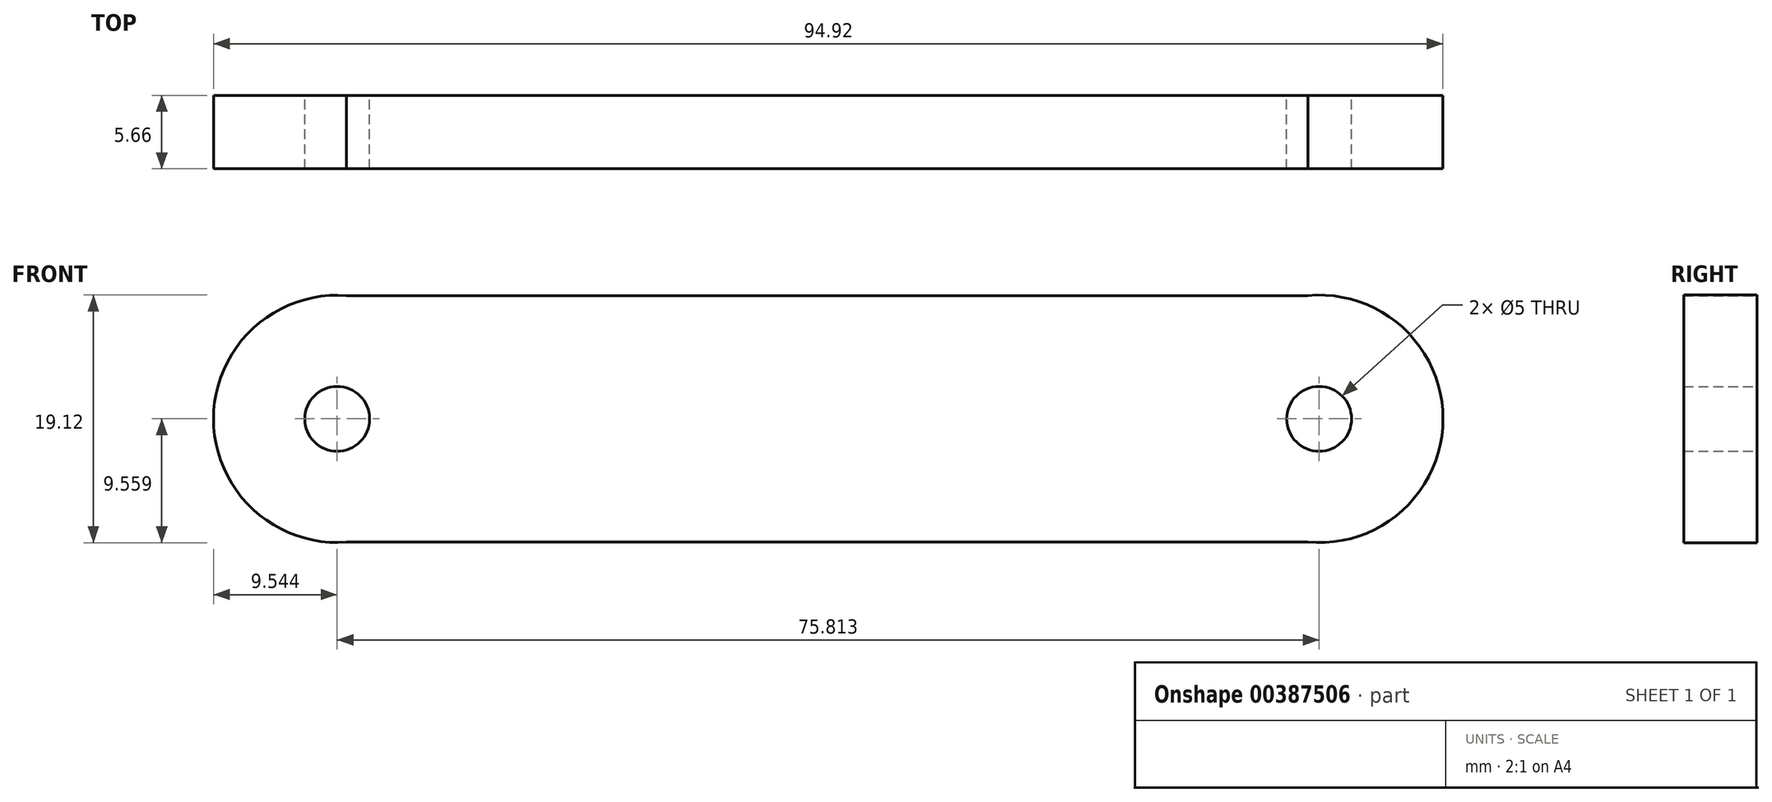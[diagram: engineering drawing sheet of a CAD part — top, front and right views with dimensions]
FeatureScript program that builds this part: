
annotation { "Feature Type Name" : "Feature", "Feature Type Description" : "" }
export const myFeature = defineFeature(function(context is Context, id is Id, definition is map)
    precondition{}
    {
        {
            var Q0;
            Q0=qCreatedBy(makeId("Front.planeOp"),FACE);
            var sketch = newSketch(context, id + "F0", { "sketchPlane" : qUnion([Q0])});
            skPoint(sketch, "E0", {"position": v(-39.05, 19.04) * mm});
            skPoint(sketch, "E1", {"position": v(35.15, 19.04) * mm});
            skPoint(sketch, "E2", {"position": v(35.15, 0) * mm});
            skPoint(sketch, "E3", {"position": v(-39.05, 0) * mm});
            skArc(sketch, "E4", {"start": v(-39.05, 19.04) * mm, "mid": v(-49.33, 9.52) * mm, "end": v(-39.05, 0) * mm});
            skArc(sketch, "E5", {"start": v(35.15, 0) * mm, "mid": v(45.59, 9.52) * mm, "end": v(35.15, 19.04) * mm});
            skLineSegment(sketch, "E6", {"start": v(-39.05, 19.04) * mm, "end": v(35.15, 19.04) * mm});
            skLineSegment(sketch, "E7", {"start": v(35.15, 0) * mm, "end": v(-39.05, 0) * mm});
            skPoint(sketch, "E8", {"position": v(-49.33, 9.52) * mm});
            skPoint(sketch, "E9", {"position": v(45.59, 9.52) * mm});
            skCircle(sketch, "E10", {"center": v(-39.79, 9.52) * mm, "radius": 2.5 * mm});
            skCircle(sketch, "E11", {"center": v(36.03, 9.52) * mm, "radius": 2.5 * mm});
            skSolve(sketch);
        }
        {
            var Q0;
            Q0 = qSketchRegion(id + "F0", true);
            extrude(context, id + "F1", {"entities" : qUnion([Q0]), "depth" : 5.66 * mm});
        }
    });
